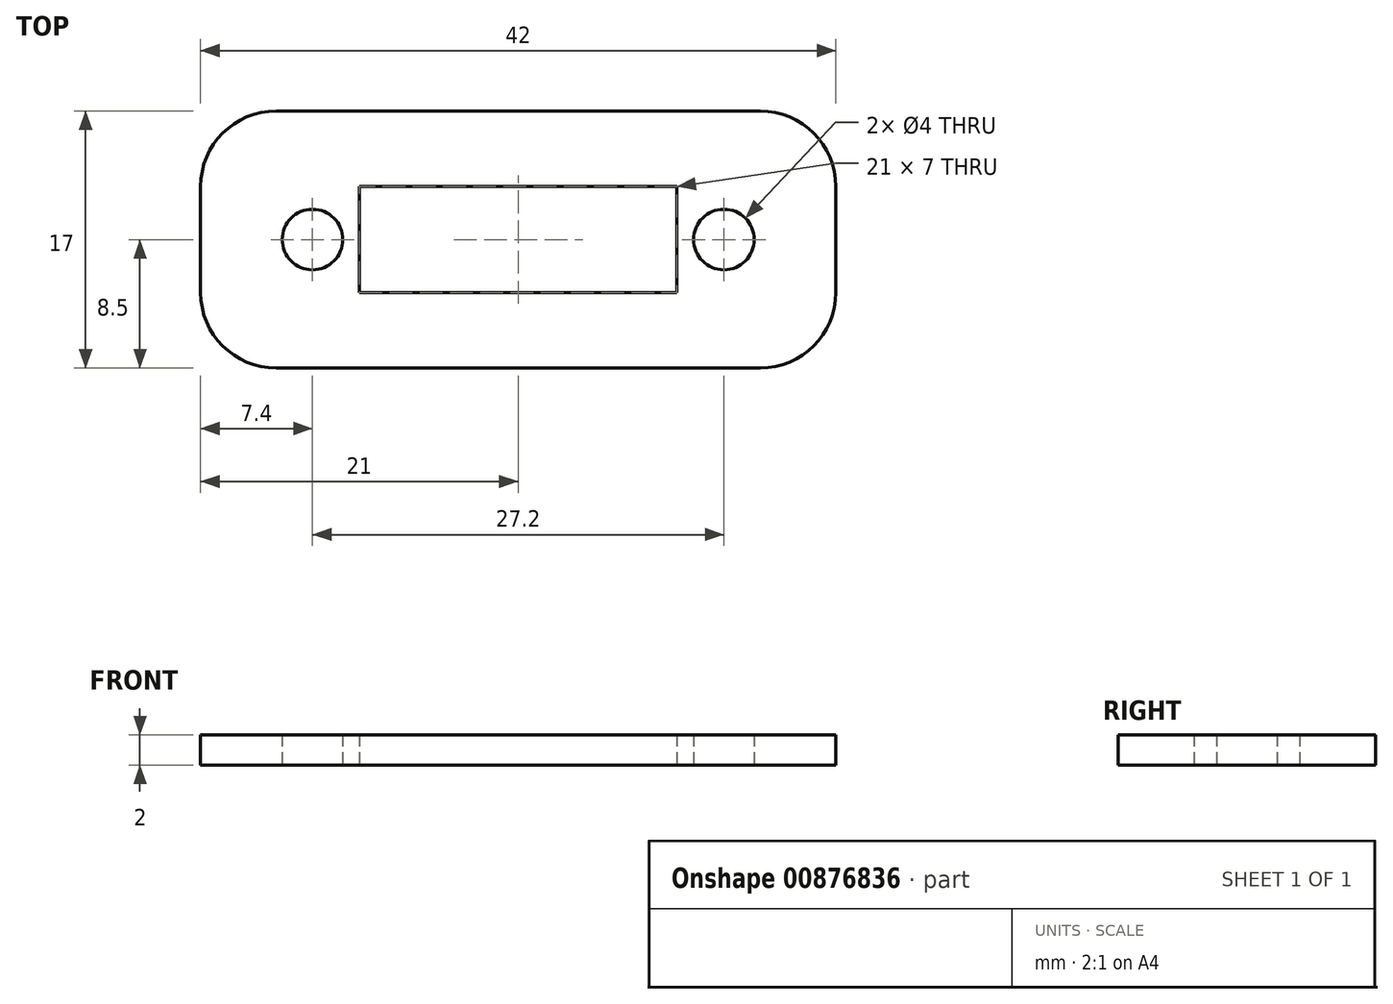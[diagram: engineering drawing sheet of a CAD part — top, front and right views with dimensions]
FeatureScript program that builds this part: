
annotation { "Feature Type Name" : "Feature", "Feature Type Description" : "" }
export const myFeature = defineFeature(function(context is Context, id is Id, definition is map)
    precondition{}
    {
        {
            var Q0;
            Q0=qCreatedBy(makeId("Top.planeOp"),FACE);
            var sketch = newSketch(context, id + "F0", { "sketchPlane" : qUnion([Q0])});
            skLineSegment(sketch, "E0.bottom", {"start": v(10.5, -3.5) * mm, "end": v(-10.5, -3.5) * mm});
            skLineSegment(sketch, "E0.top", {"start": v(10.5, 3.5) * mm, "end": v(-10.5, 3.5) * mm});
            skLineSegment(sketch, "E0.left", {"start": v(10.5, -3.5) * mm, "end": v(10.5, 3.5) * mm});
            skLineSegment(sketch, "E0.right", {"start": v(-10.5, -3.5) * mm, "end": v(-10.5, 3.5) * mm});
            skPoint(sketch, "E0.middle", {"position": v(0, 0) * mm});
            skLineSegment(sketch, "E1.bottom", {"start": v(10.5, 3.5) * mm, "end": v(16, 3.5) * mm});
            skLineSegment(sketch, "E1.top", {"start": v(10.5, -3.5) * mm, "end": v(16, -3.5) * mm});
            skLineSegment(sketch, "E1.left", {"start": v(10.5, 3.5) * mm, "end": v(10.5, -3.5) * mm});
            skLineSegment(sketch, "E1.right", {"start": v(16, 3.5) * mm, "end": v(16, -3.5) * mm});
            skCircle(sketch, "E2", {"center": v(13.6, 0) * mm, "radius": 2 * mm});
            skLineSegment(sketch, "E3.MirrorCS", {"start": v(-10.5, 3.5) * mm, "end": v(-16, 3.5) * mm});
            skLineSegment(sketch, "E4.MirrorCS", {"start": v(-10.5, -3.5) * mm, "end": v(-16, -3.5) * mm});
            skLineSegment(sketch, "E5.MirrorCS", {"start": v(-16, 3.5) * mm, "end": v(-16, -3.5) * mm});
            skCircle(sketch, "E6.MirrorC", {"center": v(-13.6, 0) * mm, "radius": 2 * mm});
            skLineSegment(sketch, "E7.0", {"start": v(10.5, 8.5) * mm, "end": v(21, 8.5) * mm});
            skLineSegment(sketch, "E7.1", {"start": v(21, 8.5) * mm, "end": v(21, -8.5) * mm});
            skLineSegment(sketch, "E7.2", {"start": v(10.5, 8.5) * mm, "end": v(-10.5, 8.5) * mm});
            skLineSegment(sketch, "E7.3", {"start": v(10.5, -8.5) * mm, "end": v(21, -8.5) * mm});
            skLineSegment(sketch, "E7.4", {"start": v(-10.5, 8.5) * mm, "end": v(-21, 8.5) * mm});
            skLineSegment(sketch, "E7.5", {"start": v(-21, 8.5) * mm, "end": v(-21, -8.5) * mm});
            skLineSegment(sketch, "E7.6", {"start": v(-10.5, -8.5) * mm, "end": v(-21, -8.5) * mm});
            skLineSegment(sketch, "E7.7", {"start": v(10.5, -8.5) * mm, "end": v(-10.5, -8.5) * mm});
            skSolve(sketch);
        }
        {
            var Q0;
            Q0=makeQuery(id+"F0.imprint","IMPRINT",FACE,{"disambiguationData":[TD([[makeQuery(id+"F0.imprint","IMPRINT",EDGE,{"derivedFrom":sQuery(id+"F0.wireOp",EDGE,"E0.bottom")}),1.0]])]});
            var Q1;
            Q1=makeQuery(id+"F0.imprint","IMPRINT",FACE,{"disambiguationData":[TD([[makeQuery(id+"F0.imprint","IMPRINT",EDGE,{"derivedFrom":sQuery(id+"F0.wireOp",EDGE,"E0.right")}),1.0]])]});
            var Q2;
            Q2=makeQuery(id+"F0.imprint","IMPRINT",FACE,{"disambiguationData":[TD([[makeQuery(id+"F0.imprint","IMPRINT",EDGE,{"derivedFrom":sQuery(id+"F0.wireOp",EDGE,"E1.bottom")}),-1.0]])]});
            extrude(context, id + "F1", {"entities" : qUnion([Q0, Q1, Q2]), "depth" : 2 * mm, "offsetDistance" : 25 * mm});
        }
        {
            var Q0;
            Q0=makeQuery(id+"F1.opExtrude","SWEPT_EDGE",EDGE,{"disambiguationData":[OSD([sQuery(id+"F0.wireOp",EDGE,"E7.4"),sQuery(id+"F0.wireOp",EDGE,"E7.5")])]});
            var Q1;
            Q1=makeQuery(id+"F1.opExtrude","SWEPT_EDGE",EDGE,{"disambiguationData":[OSD([sQuery(id+"F0.wireOp",EDGE,"E7.5"),sQuery(id+"F0.wireOp",EDGE,"E7.6")])]});
            var Q2;
            Q2=makeQuery(id+"F1.opExtrude","SWEPT_EDGE",EDGE,{"disambiguationData":[OSD([sQuery(id+"F0.wireOp",EDGE,"E7.1"),sQuery(id+"F0.wireOp",EDGE,"E7.3")])]});
            var Q3;
            Q3=makeQuery(id+"F1.opExtrude","SWEPT_EDGE",EDGE,{"disambiguationData":[OSD([sQuery(id+"F0.wireOp",EDGE,"E7.0"),sQuery(id+"F0.wireOp",EDGE,"E7.1")])]});
            fillet(context, id + "F2", {"entities" : qUnion([Q0, Q1, Q2, Q3]), "radius" : 5 * mm, "tangentPropagation" : true, "allowEdgeOverflow" : false});
        }
    });
